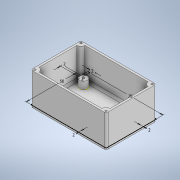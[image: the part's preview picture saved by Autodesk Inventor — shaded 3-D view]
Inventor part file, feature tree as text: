
AUTODESK INVENTOR PART (.ipt)
format: ipt  version: 2020.2 (Build 242310000, 310)  size: 238,080 bytes
history: native  units: mm
features: extrude x4, sketch x3, fillet x2
ambient origin geometry x8: Origin, YZ Plane, XZ Plane, XY Plane, X Axis, Y Axis, Z Axis, Center Point
bodies: Solid1 (feature_tree)
feature tree (9):
  extrude  "Extrusion1"  Depth=53.0mm
  sketch  "Sketch2"  dims[d2=2.0mm d3=7.5mm]
  extrude  "Extrusion7"  Depth=2.0mm
  extrude  "Extrusion8"  Depth=2.0mm
  extrude  "Extrusion9"  Depth=2.0mm
  fillet  "Fillet2"  Radius=2.0mm
  fillet  "Fillet3"  Radius=2.0mm
  sketch  "Sketch1"  dims[d0=33.0mm d1=53.0mm]
  sketch  "Sketch6"  dims[d4=7.5mm d5=0.0mm d6=75.0mm d10=50.0mm d11=2.0mm d24=2.0mm d129=4.0mm d132=2.0mm d133=2.0mm d134=2.0mm d135=2.0mm d136=0.0mm d137=30.0mm d138=0.0mm d139=10.0mm d140=0.0mm d141=2.0mm d142=2.0mm d28=0.5mm d29=0.872665mm d30=0.5mm d31=0.872665mm]
